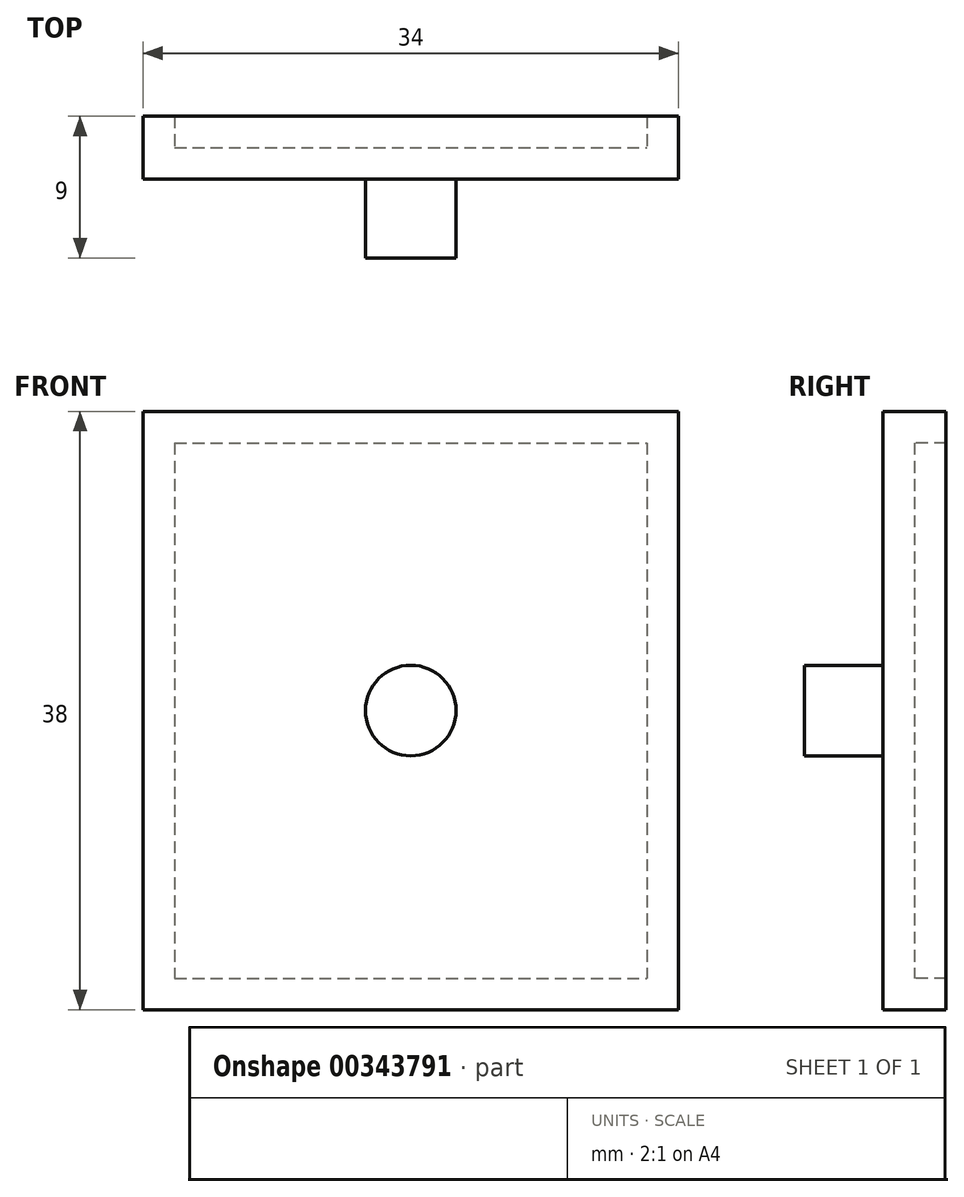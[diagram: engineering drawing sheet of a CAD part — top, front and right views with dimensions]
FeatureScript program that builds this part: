
annotation { "Feature Type Name" : "Feature", "Feature Type Description" : "" }
export const myFeature = defineFeature(function(context is Context, id is Id, definition is map)
    precondition{}
    {
        {
            var Q0;
            Q0=qCreatedBy(makeId("Front.planeOp"),FACE);
            var sketch = newSketch(context, id + "F0", { "sketchPlane" : qUnion([Q0])});
            skLineSegment(sketch, "E0.bottom", {"start": v(-17, 19) * mm, "end": v(17, 19) * mm});
            skLineSegment(sketch, "E0.top", {"start": v(-17, -19) * mm, "end": v(17, -19) * mm});
            skLineSegment(sketch, "E0.left", {"start": v(-17, 19) * mm, "end": v(-17, -19) * mm});
            skLineSegment(sketch, "E0.right", {"start": v(17, 19) * mm, "end": v(17, -19) * mm});
            skPoint(sketch, "E0.middle", {"position": v(0, 0) * mm});
            skLineSegment(sketch, "E1.bottom", {"start": v(-15, 17) * mm, "end": v(15, 17) * mm});
            skLineSegment(sketch, "E1.top", {"start": v(-15, -17) * mm, "end": v(15, -17) * mm});
            skLineSegment(sketch, "E1.left", {"start": v(-15, 17) * mm, "end": v(-15, -17) * mm});
            skLineSegment(sketch, "E1.right", {"start": v(15, 17) * mm, "end": v(15, -17) * mm});
            skSolve(sketch);
        }
        {
            var Q0;
            Q0=makeQuery(id+"F0.imprint","IMPRINT",FACE,{"disambiguationData":[TD([[makeQuery(id+"F0.imprint","IMPRINT",EDGE,{"derivedFrom":sQuery(id+"F0.wireOp",EDGE,"E1.bottom")}),-1.0]])]});
            var Q1;
            Q1=makeQuery(id+"F0.imprint","IMPRINT",FACE,{"disambiguationData":[TD([[makeQuery(id+"F0.imprint","IMPRINT",EDGE,{"derivedFrom":sQuery(id+"F0.wireOp",EDGE,"E0.bottom")}),-1.0]])]});
            extrude(context, id + "F1", {"entities" : qUnion([Q0, Q1]), "depth" : 2 * mm, "offsetDistance" : 25 * mm});
        }
        {
            var Q0;
            Q0=qCreatedBy(makeId("Front.planeOp"),FACE);
            var sketch = newSketch(context, id + "F2", { "sketchPlane" : qUnion([Q0])});
            skCircle(sketch, "E2", {"center": v(0, 0) * mm, "radius": 2.87 * mm});
            skSolve(sketch);
        }
        {
            var Q0;
            Q0 = qSketchRegion(id + "F2", true);
            extrude(context, id + "F3", {"entities" : qUnion([Q0]), "operationType" : NewBodyOperationType.ADD, "depth" : 7 * mm, "offsetDistance" : 25 * mm});
        }
        {
            var Q0;
            Q0 = qSketchRegion(id + "F0", true);
            extrude(context, id + "F4", {"entities" : qUnion([Q0]), "operationType" : NewBodyOperationType.ADD, "oppositeDirection" : true, "depth" : 2 * mm, "offsetDistance" : 25 * mm});
        }
    });
